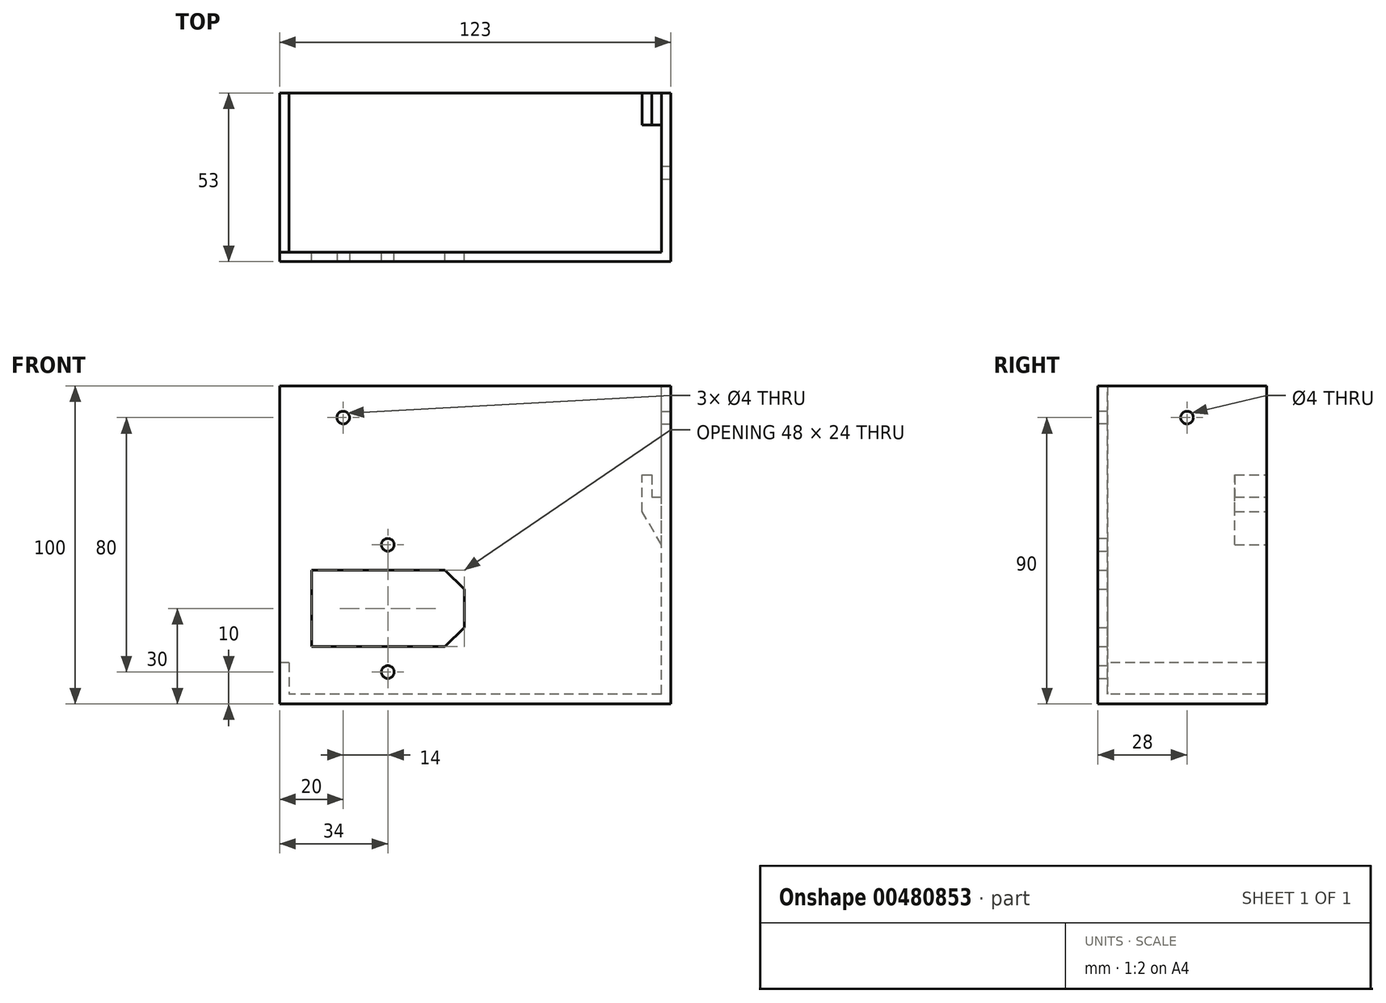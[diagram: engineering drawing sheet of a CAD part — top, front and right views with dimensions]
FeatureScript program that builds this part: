
annotation { "Feature Type Name" : "Feature", "Feature Type Description" : "" }
export const myFeature = defineFeature(function(context is Context, id is Id, definition is map)
    precondition{}
    {
        {
            var Q0;
            Q0=qCreatedBy(makeId("Front.planeOp"),FACE);
            var sketch = newSketch(context, id + "F0", { "sketchPlane" : qUnion([Q0])});
            skLineSegment(sketch, "E0.bottom", {"start": v(0, 0) * mm, "end": v(123, 0) * mm});
            skLineSegment(sketch, "E0.top", {"start": v(0, -100) * mm, "end": v(123, -100) * mm});
            skLineSegment(sketch, "E0.left", {"start": v(0, 0) * mm, "end": v(0, -100) * mm});
            skLineSegment(sketch, "E0.right", {"start": v(123, 0) * mm, "end": v(123, -100) * mm});
            skLineSegment(sketch, "E1.bottom", {"start": v(10, -58) * mm, "end": v(52, -58) * mm});
            skLineSegment(sketch, "E1.top", {"start": v(10, -82) * mm, "end": v(52, -82) * mm});
            skLineSegment(sketch, "E1.left", {"start": v(10, -58) * mm, "end": v(10, -82) * mm});
            skLineSegment(sketch, "E1.right", {"start": v(58, -64) * mm, "end": v(58, -76) * mm});
            skLineSegment(sketch, "E2", {"start": v(52, -58) * mm, "end": v(58, -64) * mm});
            skLineSegment(sketch, "E3", {"start": v(12.4, -70) * mm, "end": v(56.14, -70) * mm, "construction": true});
            skPoint(sketch, "E3.endSnap0", {"position": v(58, -70) * mm});
            skLineSegment(sketch, "E4.MirrorCS", {"start": v(52, -82) * mm, "end": v(58, -76) * mm});
            skPoint(sketch, "E5.orphan", {"position": v(58, -58) * mm});
            skPoint(sketch, "E6.orphan", {"position": v(58, -82) * mm});
            skCircle(sketch, "E7", {"center": v(34, -50) * mm, "radius": 2 * mm});
            skCircle(sketch, "E8.MirrorC", {"center": v(34, -90) * mm, "radius": 2 * mm});
            skLineSegment(sketch, "E9", {"start": v(34, -50) * mm, "end": v(34, -90) * mm, "construction": true});
            skSolve(sketch);
        }
        {
            var Q0;
            Q0 = qSketchRegion(id + "F0", true);
            extrude(context, id + "F1", {"entities" : qUnion([Q0]), "depth" : 3 * mm});
        }
        {
            var Q0;
            Q0=makeQuery(id+"F1.opExtrude","CAP_FACE",FACE,{"disambiguationData":[OSD([sQuery(id+"F0.wireOp",EDGE,"E0.bottom"),sQuery(id+"F0.wireOp",EDGE,"E0.top"),sQuery(id+"F0.wireOp",EDGE,"E0.left"),sQuery(id+"F0.wireOp",EDGE,"E0.right"),sQuery(id+"F0.wireOp",EDGE,"E1.bottom"),sQuery(id+"F0.wireOp",EDGE,"E1.top"),sQuery(id+"F0.wireOp",EDGE,"E1.left"),sQuery(id+"F0.wireOp",EDGE,"E1.right"),sQuery(id+"F0.wireOp",EDGE,"E2"),sQuery(id+"F0.wireOp",EDGE,"E4.MirrorCS"),sQuery(id+"F0.wireOp",EDGE,"E7"),sQuery(id+"F0.wireOp",EDGE,"E8.MirrorC")])],"isStart":true});
            var sketch = newSketch(context, id + "F2", { "sketchPlane" : qUnion([Q0])});
            skLineSegment(sketch, "E10.bottom", {"start": v(-123, -100) * mm, "end": v(-120, -100) * mm});
            skLineSegment(sketch, "E10.top", {"start": v(-123, 0) * mm, "end": v(-120, 0) * mm});
            skLineSegment(sketch, "E10.left", {"start": v(-123, -100) * mm, "end": v(-123, 0) * mm});
            skLineSegment(sketch, "E10.right", {"start": v(-120, -100) * mm, "end": v(-120, 0) * mm});
            skSolve(sketch);
        }
        {
            var Q0;
            Q0 = qSketchRegion(id + "F2", true);
            extrude(context, id + "F3", {"entities" : qUnion([Q0]), "operationType" : NewBodyOperationType.ADD, "depth" : 50 * mm});
        }
        {
            var Q0;
            Q0=makeQuery(id+"F1.opExtrude","CAP_FACE",FACE,{"disambiguationData":[OSD([sQuery(id+"F0.wireOp",EDGE,"E0.bottom"),sQuery(id+"F0.wireOp",EDGE,"E0.top"),sQuery(id+"F0.wireOp",EDGE,"E0.left"),sQuery(id+"F0.wireOp",EDGE,"E0.right"),sQuery(id+"F0.wireOp",EDGE,"E1.bottom"),sQuery(id+"F0.wireOp",EDGE,"E1.top"),sQuery(id+"F0.wireOp",EDGE,"E1.left"),sQuery(id+"F0.wireOp",EDGE,"E1.right"),sQuery(id+"F0.wireOp",EDGE,"E2"),sQuery(id+"F0.wireOp",EDGE,"E4.MirrorCS"),sQuery(id+"F0.wireOp",EDGE,"E7"),sQuery(id+"F0.wireOp",EDGE,"E8.MirrorC")])],"isStart":true});
            var sketch = newSketch(context, id + "F4", { "sketchPlane" : qUnion([Q0])});
            skLineSegment(sketch, "E11.bottom", {"start": v(-120, -100) * mm, "end": v(0, -100) * mm});
            skLineSegment(sketch, "E11.top", {"start": v(-120, -97) * mm, "end": v(0, -97) * mm});
            skLineSegment(sketch, "E11.left", {"start": v(-120, -100) * mm, "end": v(-120, -97) * mm});
            skLineSegment(sketch, "E11.right", {"start": v(0, -100) * mm, "end": v(0, -97) * mm});
            skSolve(sketch);
        }
        {
            var Q0;
            Q0 = qSketchRegion(id + "F4", true);
            extrude(context, id + "F5", {"entities" : qUnion([Q0]), "operationType" : NewBodyOperationType.ADD, "depth" : 50 * mm});
        }
        {
            var Q0;
            Q0=makeQuery(id+"F1.opExtrude","CAP_FACE",FACE,{"disambiguationData":[OSD([sQuery(id+"F0.wireOp",EDGE,"E0.bottom"),sQuery(id+"F0.wireOp",EDGE,"E0.top"),sQuery(id+"F0.wireOp",EDGE,"E0.left"),sQuery(id+"F0.wireOp",EDGE,"E0.right"),sQuery(id+"F0.wireOp",EDGE,"E1.bottom"),sQuery(id+"F0.wireOp",EDGE,"E1.top"),sQuery(id+"F0.wireOp",EDGE,"E1.left"),sQuery(id+"F0.wireOp",EDGE,"E1.right"),sQuery(id+"F0.wireOp",EDGE,"E2"),sQuery(id+"F0.wireOp",EDGE,"E4.MirrorCS"),sQuery(id+"F0.wireOp",EDGE,"E7"),sQuery(id+"F0.wireOp",EDGE,"E8.MirrorC")])],"isStart":false});
            var sketch = newSketch(context, id + "F6", { "sketchPlane" : qUnion([Q0])});
            skCircle(sketch, "E12", {"center": v(20, -10) * mm, "radius": 2 * mm});
            skSolve(sketch);
        }
        {
            var Q0;
            Q0 = qSketchRegion(id + "F6", true);
            extrude(context, id + "F7", {"entities" : qUnion([Q0]), "operationType" : NewBodyOperationType.REMOVE, "endBound" : BoundingType.THROUGH_ALL, "oppositeDirection" : true, "depth" : 25 * mm});
        }
        {
            var Q0;
            Q0=makeQuery(id+"F3.boolean.opBoolean","MERGE",FACE,{"derivedFrom":[makeQuery(id+"F1.opExtrude","SWEPT_FACE",FACE,{"disambiguationData":[OSD([sQuery(id+"F0.wireOp",EDGE,"E0.right")])]}),makeQuery(id+"F3.opExtrude","SWEPT_FACE",FACE,{"disambiguationData":[OSD([sQuery(id+"F2.wireOp",EDGE,"E10.left")])]})]});
            var sketch = newSketch(context, id + "F8", { "sketchPlane" : qUnion([Q0])});
            skCircle(sketch, "E13", {"center": v(25, -10) * mm, "radius": 2 * mm});
            skSolve(sketch);
        }
        {
            var Q0;
            Q0 = qSketchRegion(id + "F8", true);
            extrude(context, id + "F9", {"entities" : qUnion([Q0]), "operationType" : NewBodyOperationType.REMOVE, "endBound" : BoundingType.THROUGH_ALL, "oppositeDirection" : true, "depth" : 25 * mm});
        }
        {
            var Q0;
            Q0=makeQuery(id+"F5.opExtrude","SWEPT_FACE",FACE,{"disambiguationData":[OSD([sQuery(id+"F4.wireOp",EDGE,"E11.top")])]});
            var sketch = newSketch(context, id + "F10", { "sketchPlane" : qUnion([Q0])});
            skLineSegment(sketch, "E14.bottom", {"start": v(0, 0) * mm, "end": v(3, 0) * mm});
            skLineSegment(sketch, "E14.top", {"start": v(0, 50) * mm, "end": v(3, 50) * mm});
            skLineSegment(sketch, "E14.left", {"start": v(0, 0) * mm, "end": v(0, 50) * mm});
            skLineSegment(sketch, "E14.right", {"start": v(3, 0) * mm, "end": v(3, 50) * mm});
            skSolve(sketch);
        }
        {
            var Q0;
            Q0 = qSketchRegion(id + "F10", true);
            extrude(context, id + "F11", {"entities" : qUnion([Q0]), "operationType" : NewBodyOperationType.ADD, "depth" : 10 * mm});
        }
        {
            var Q0;
            Q0=makeQuery(id+"F11.boolean.opBoolean","MERGE",FACE,{"derivedFrom":[makeQuery(id+"F5.boolean.opBoolean","MERGE",FACE,{"derivedFrom":[makeQuery(id+"F3.opExtrude","CAP_FACE",FACE,{"disambiguationData":[OSD([sQuery(id+"F2.wireOp",EDGE,"E10.bottom"),sQuery(id+"F2.wireOp",EDGE,"E10.top"),sQuery(id+"F2.wireOp",EDGE,"E10.left"),sQuery(id+"F2.wireOp",EDGE,"E10.right")])],"isStart":false}),makeQuery(id+"F5.opExtrude","CAP_FACE",FACE,{"disambiguationData":[OSD([sQuery(id+"F4.wireOp",EDGE,"E11.bottom"),sQuery(id+"F4.wireOp",EDGE,"E11.top"),sQuery(id+"F4.wireOp",EDGE,"E11.left"),sQuery(id+"F4.wireOp",EDGE,"E11.right")])],"isStart":false})]}),makeQuery(id+"F11.opExtrude","SWEPT_FACE",FACE,{"disambiguationData":[OSD([sQuery(id+"F10.wireOp",EDGE,"E14.top")])]})]});
            var sketch = newSketch(context, id + "F12", { "sketchPlane" : qUnion([Q0])});
            skLineSegment(sketch, "E15", {"start": v(-120, -50) * mm, "end": v(-114, -39.6) * mm});
            skLineSegment(sketch, "E16", {"start": v(-114, -39.6) * mm, "end": v(-114, -28) * mm});
            skLineSegment(sketch, "E17", {"start": v(-114, -28) * mm, "end": v(-117, -28) * mm});
            skLineSegment(sketch, "E18", {"start": v(-117, -28) * mm, "end": v(-117, -35) * mm});
            skLineSegment(sketch, "E19", {"start": v(-117, -35) * mm, "end": v(-120, -35) * mm});
            skLineSegment(sketch, "E20", {"start": v(-120, -35) * mm, "end": v(-120, -50) * mm});
            skSolve(sketch);
        }
        {
            var Q0;
            Q0 = qSketchRegion(id + "F12", true);
            extrude(context, id + "F13", {"entities" : qUnion([Q0]), "operationType" : NewBodyOperationType.ADD, "oppositeDirection" : true, "depth" : 10 * mm});
        }
    });
